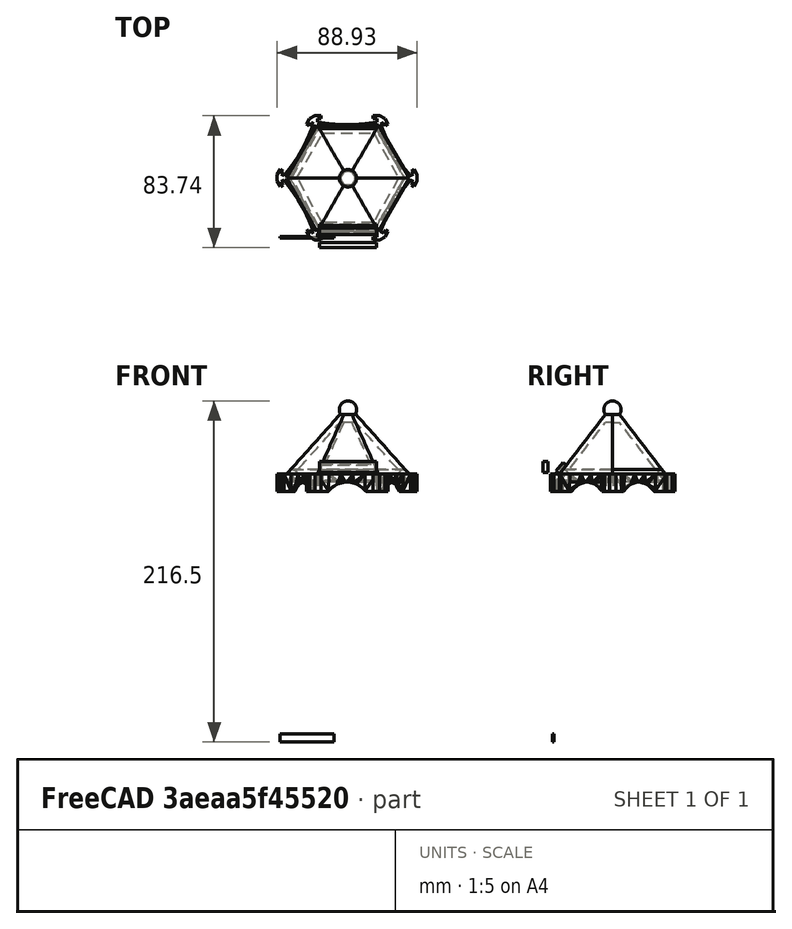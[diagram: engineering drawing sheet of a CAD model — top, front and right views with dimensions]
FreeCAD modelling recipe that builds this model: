
FCSTD DOCUMENT  (FreeCAD 0.16R)
Label: techo reparado exagono
License: All rights reserved
LicenseURL: http://en.wikipedia.org/wiki/All_rights_reserved
objects: Part::Feature×6, Sketcher::SketchObject×3, Part::RegularPolygon×2, Part::MultiFuse×2, Part::Loft×1, Part::Sphere×1, Part::Cylinder×1, PartDesign::Pad×1, Part::Thickness×1, Part::Box×1, PartDesign::Pocket×1
note: 22 computed .brp shape members not serialized (recipe doc carries the construction recipe); baked Part::Feature solids carry a one-line shape summary decoded from their .brp

FEATURE [Part::RegularPolygon] RegularPolygon001  label="Polígono regular001"
  Circumradius = 39
  Placement = pos=(44,39,167) rot=(0,0,1;0rad)
  Polygon = 6
FEATURE [Part::RegularPolygon] RegularPolygon002  label="Polígono regular002"
  Circumradius = 5
  Placement = pos=(44,39,205) rot=(0,0,1;0rad)
  Polygon = 6
FEATURE [Part::Feature] Cut  label="Cut003"
  Placement = pos=(-0.942682,-0.269107,0) rot=(0,0,1;0rad)
  shape: bbox 88.93 x 79.01 x 11 mm, 641 faces (baked)
FEATURE [Part::Loft] Loft
  Closed = true
  Ruled = true
  Sections = -> [RegularPolygon001,RegularPolygon002]
  Solid = true
FEATURE [Part::Feature] Face
  shape: bbox 10 x 8.66 x 2e-07 mm, 1 faces, 0 solids (baked)
FEATURE [Part::Feature] Face001
  shape: bbox 78 x 67.55 x 2e-07 mm, 1 faces, 0 solids (baked)
FEATURE [Part::Feature] Shell
  Placement = pos=(0,0,5) rot=(0,0,1;0rad)
  shape: bbox 78 x 67.55 x 38 mm, 8 faces, 0 solids (baked)
FEATURE [Part::Sphere] Sphere  label="Esfera"
  Angle1 = -90
  Angle2 = 90
  Angle3 = 360
  Placement = pos=(44,39,213) rot=(0,0,1;0rad)
  Radius = 5.5
FEATURE [Part::Cylinder] Cylinder  label="Cilindro"
  Angle = 360
  Height = 10
  Placement = pos=(44,39,205) rot=(0,0,1;0rad)
  Radius = 3
FEATURE [Part::MultiFuse] Fusion
  Shapes = -> [Cylinder,Sphere]
FEATURE [Part::Feature] Solid
  shape: bbox 78 x 67.55 x 38 mm, 8 faces (baked)
FEATURE [Part::MultiFuse] Fusion001
  Shapes = -> [Solid,Fusion]
FEATURE [Sketcher::SketchObject] Sketch
  Placement = pos=(0,0,172) rot=(1,0,0;3.14159rad)
  Support = -> Fusion001 [Face1]
  sketch-geometry (6):
    g0: LineSegment StartX=61.7849 StartY=-7.72586 StartZ=0 EndX=25.7467 EndY=-7.72586 EndZ=0
    g1: LineSegment StartX=25.7467 StartY=-7.72586 StartZ=0 EndX=8.36928 EndY=-39.2977 EndZ=0
    g2: LineSegment StartX=8.36928 StartY=-39.2977 StartZ=0 EndX=26.2302 EndY=-70.5985 EndZ=0
    g3: LineSegment StartX=26.2302 StartY=-70.5985 StartZ=0 EndX=62.2684 EndY=-70.5985 EndZ=0
    g4: LineSegment StartX=62.2684 StartY=-70.5985 StartZ=0 EndX=79.6458 EndY=-39.0267 EndZ=0
    g5: LineSegment StartX=79.6458 StartY=-39.0267 StartZ=0 EndX=61.7849 EndY=-7.72586 EndZ=0
  constraints (9):
    c: Coincident(g0,g1)
    c: Coincident(g1,g2)
    c: Coincident(g2,g3)
    c: Coincident(g3,g4)
    c: Coincident(g4,g5)
    c: Coincident(g5,g0)
    c: Equal(g0, g1-g5) x5
    c: Horizontal(g0)
    c: Horizontal(g3)
FEATURE [PartDesign::Pad] Pad
  Length = 4
  Length2 = 100
  Sketch = -> Sketch
  Type = 0
FEATURE [Part::Thickness] Thickness
  Faces = -> Pad [Face1]
  Intersection = false
  Join = 0
  Mode = 0
  SelfIntersection = false
  Value = -3
FEATURE [Part::Box] Box  label="Cubo"
  Height = 7
  Length = 36
  Placement = pos=(26,-5,173) rot=(0,0,1;0rad)
  Width = 3
FEATURE [Sketcher::SketchObject] Sketch001
  ExternalGeometry = -> [Box]
  Placement = pos=(26,-5,180) rot=(0,0,1;0rad)
  Support = -> Box [Face6]
  sketch-geometry (4):
    g0: LineSegment StartX=1 StartY=2 StartZ=0 EndX=35 EndY=2 EndZ=0
    g1: LineSegment StartX=35 StartY=2 StartZ=0 EndX=35 EndY=1 EndZ=0
    g2: LineSegment StartX=35 StartY=1 StartZ=0 EndX=1 EndY=1 EndZ=0
    g3: LineSegment StartX=1 StartY=1 StartZ=0 EndX=1 EndY=2 EndZ=0
  constraints (12):
    c: Coincident(g0,g1)
    c: Coincident(g1,g2)
    c: Coincident(g2,g3)
    c: Coincident(g3,g0)
    c: Horizontal(g0)
    c: Horizontal(g2)
    c: Vertical(g1)
    c: Vertical(g3)
    c: DistanceY(g0,g-3) = 1
    c: DistanceY(g-4,g1) = 1
    c: DistanceX(g1,g-4) = 1
    c: DistanceX(g-1,g2) = 1
FEATURE [PartDesign::Pocket] Pocket
  Length = 5
  Placement = pos=(26,-5,173) rot=(0,0,1;0rad)
  Sketch = -> Sketch001
  Type = 0
FEATURE [Part::Feature] Pocket002
  Placement = pos=(26,3.22501,174) rot=(-1,0,0;0.645772rad)
  shape: bbox 36 x 6.609 x 7.396 mm, 11 faces (baked)
FEATURE [Sketcher::SketchObject] Sketch002
  ExternalGeometry = -> [Thickness]
  Placement = pos=(0,0,168) rot=(1,0,0;3.14159rad)
  Support = -> Thickness [Face21]
  sketch-geometry (4):
    g0: LineSegment StartX=26.7467 StartY=-8.72586 StartZ=0 EndX=60.7849 EndY=-8.72586 EndZ=0
    g1: LineSegment StartX=60.7849 StartY=-8.72586 StartZ=0 EndX=60.7849 EndY=-9.72586 EndZ=0
    g2: LineSegment StartX=60.7849 StartY=-9.72586 StartZ=0 EndX=26.7467 EndY=-9.72586 EndZ=0
    g3: LineSegment StartX=26.7467 StartY=-9.72586 StartZ=0 EndX=26.7467 EndY=-8.72586 EndZ=0
  constraints (12):
    c: Coincident(g0,g1)
    c: Coincident(g1,g2)
    c: Coincident(g2,g3)
    c: Coincident(g3,g0)
    c: Horizontal(g0)
    c: Horizontal(g2)
    c: Vertical(g1)
    c: Vertical(g3)
    c: DistanceY(g0,g-3) = 1
    c: DistanceY(g1,g1) = 1
    c: DistanceX(g0,g-3) = 1
    c: DistanceX(g-3,g0) = 1
